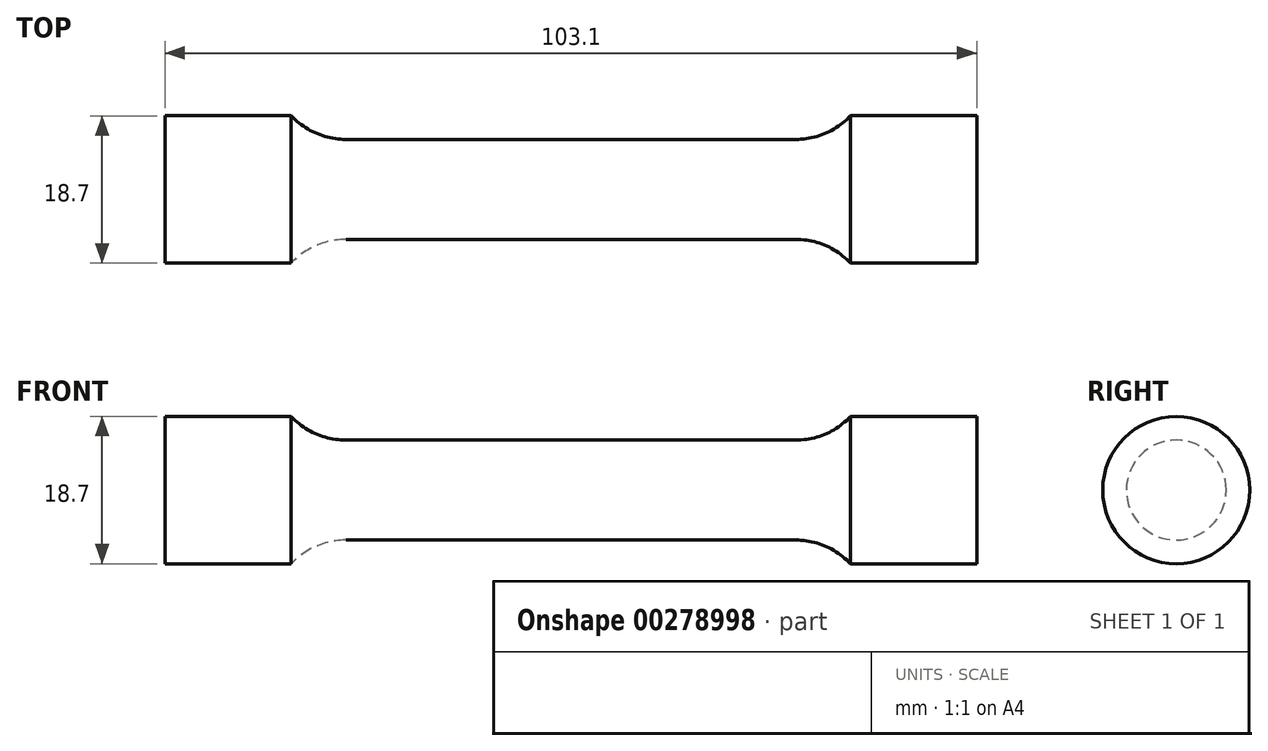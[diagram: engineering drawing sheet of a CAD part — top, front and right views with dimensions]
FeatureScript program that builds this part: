
annotation { "Feature Type Name" : "Feature", "Feature Type Description" : "" }
export const myFeature = defineFeature(function(context is Context, id is Id, definition is map)
    precondition{}
    {
        {
            var Q0;
            Q0=qCreatedBy(makeId("Front.planeOp"),FACE);
            var sketch = newSketch(context, id + "F0", { "sketchPlane" : qUnion([Q0])});
            skLineSegment(sketch, "E0", {"start": v(0, 6.35) * mm, "end": v(28.58, 6.35) * mm});
            skArc(sketch, "E1", {"start": v(28.58, 6.35) * mm, "mid": v(32.36, 7.13) * mm, "end": v(35.52, 9.35) * mm});
            skLineSegment(sketch, "E2", {"start": v(35.52, 9.35) * mm, "end": v(51.55, 9.35) * mm});
            skLineSegment(sketch, "E3", {"start": v(51.55, 9.35) * mm, "end": v(51.55, 0) * mm});
            skLineSegment(sketch, "E4.MirrorCS", {"start": v(0, 6.35) * mm, "end": v(-28.58, 6.35) * mm});
            skLineSegment(sketch, "E5.MirrorCS", {"start": v(-51.55, 9.35) * mm, "end": v(-51.55, 0) * mm});
            skLineSegment(sketch, "E6.MirrorCS", {"start": v(-35.52, 9.35) * mm, "end": v(-51.55, 9.35) * mm});
            skArc(sketch, "E7.MirrorCS", {"start": v(-28.58, 6.35) * mm, "mid": v(-32.36, 7.13) * mm, "end": v(-35.52, 9.35) * mm});
            skLineSegment(sketch, "E8", {"start": v(-51.55, 0) * mm, "end": v(51.55, 0) * mm});
            skSolve(sketch);
        }
        {
            var Q0;
            Q0 = qSketchRegion(id + "F0", true);
            var Q1;
            Q1=sQuery(id+"F0.wireOp",EDGE,"E8");
            revolve(context, id + "F1", {"entities" : qUnion([Q0]), "axis" : qUnion([Q1]), "revolveType" : RevolveType.FULL});
        }
    });
